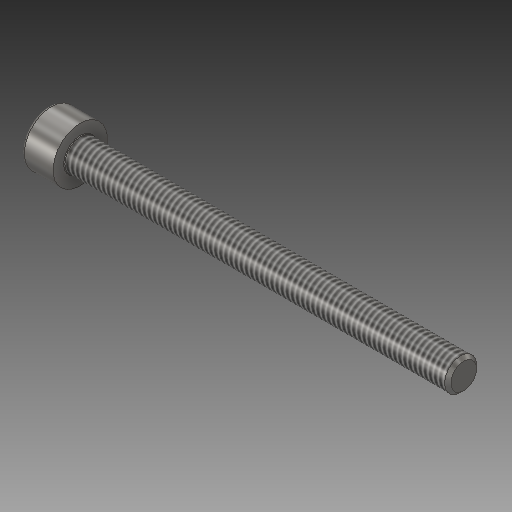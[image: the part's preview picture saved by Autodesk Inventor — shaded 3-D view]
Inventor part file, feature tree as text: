
AUTODESK INVENTOR PART (.ipt)
format: ipt  version: 2018 (Build 220112000, 112)  size: 194,560 bytes
history: native  units: mm
features: other x6, sketch x2, plane x1
ambient origin geometry x8: Origin, YZ Plane, XZ Plane, XY Plane, X Axis, Y Axis, Z Axis, Center Point
bodies: Solid1 (feature_tree)
feature tree (9):
  other  "Forged Socket Head Cap Screw - Metric M5x0.8 x 60"
  other  "Solid1::Forged Socket Head Cap Screw - Metric M5x0.8 x 60"
  other  "TaggingFeature1"
  sketch  "Sketch1"  dims[d0=10.0mm]
  sketch  "Sketch2"  dims[d19=0.0mm d28=0.0mm d29=0.0mm]
  plane  "Work Plane1"
  other  "Align 2D"
  other  "Align1"
  other  "Insert In1"
